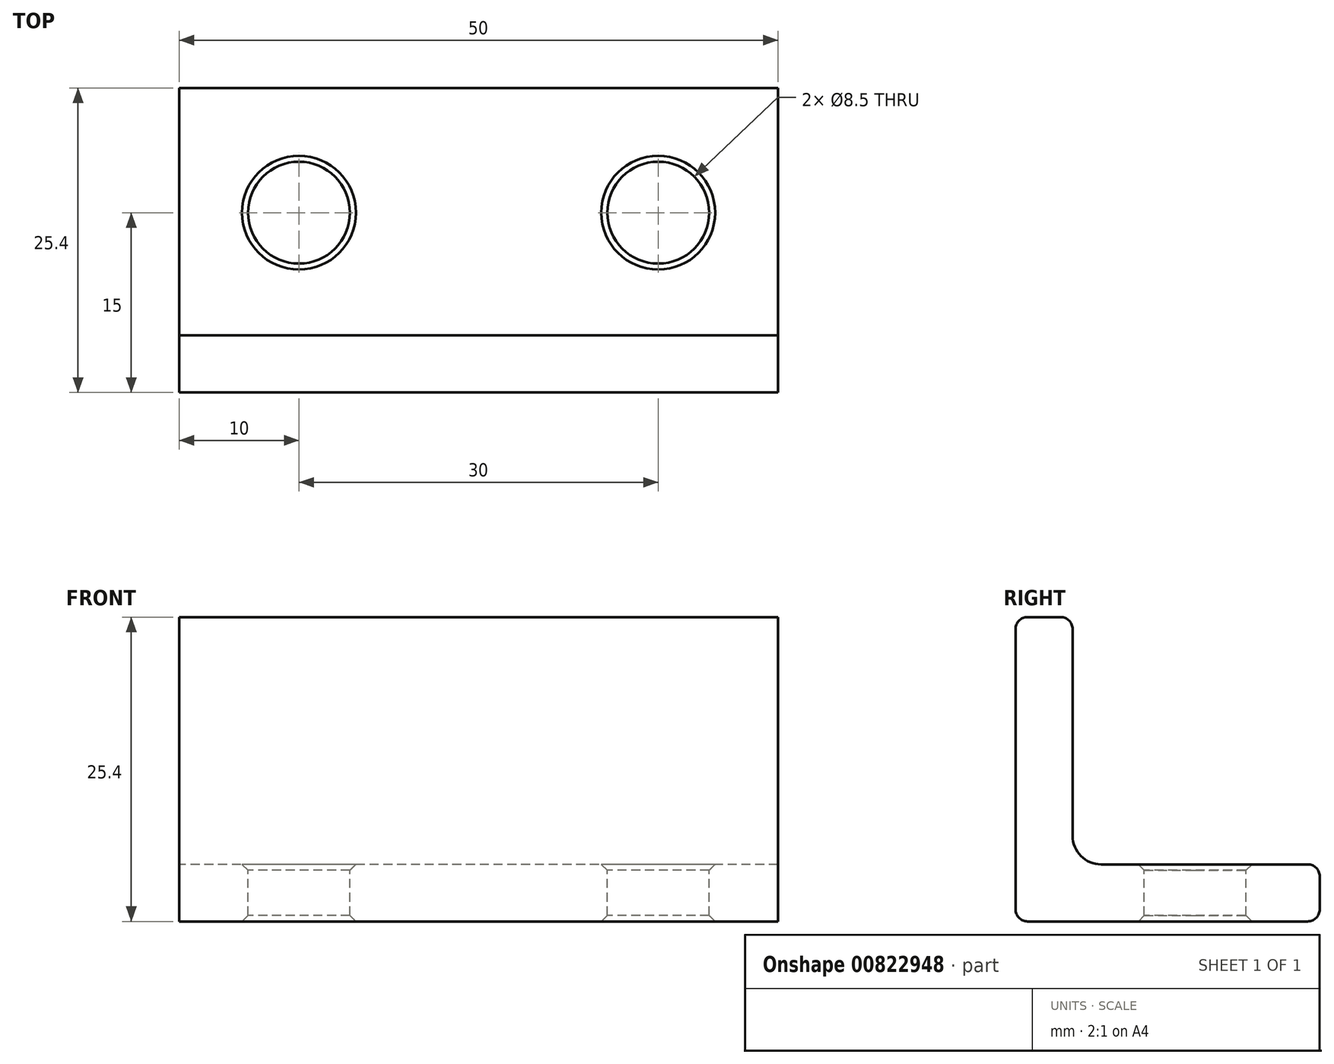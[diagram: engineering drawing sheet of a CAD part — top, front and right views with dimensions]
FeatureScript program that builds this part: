
annotation { "Feature Type Name" : "Feature", "Feature Type Description" : "" }
export const myFeature = defineFeature(function(context is Context, id is Id, definition is map)
    precondition{}
    {
        {
            var Q0;
            Q0=qCreatedBy(makeId("Right.planeOp"),FACE);
            var sketch = newSketch(context, id + "F0", { "sketchPlane" : qUnion([Q0])});
            skLineSegment(sketch, "E0", {"start": v(0, 0) * mm, "end": v(25.4, 0) * mm});
            skLineSegment(sketch, "E1", {"start": v(0, 0) * mm, "end": v(0, 25.4) * mm});
            skLineSegment(sketch, "E2", {"start": v(0, 25.4) * mm, "end": v(4.76, 25.4) * mm});
            skLineSegment(sketch, "E3", {"start": v(4.76, 25.4) * mm, "end": v(4.76, 4.76) * mm});
            skLineSegment(sketch, "E4", {"start": v(4.76, 4.76) * mm, "end": v(25.4, 4.76) * mm});
            skLineSegment(sketch, "E5", {"start": v(25.4, 4.76) * mm, "end": v(25.4, 0) * mm});
            skSolve(sketch);
        }
        {
            var Q0;
            Q0=qSketchRegion(id+"F0",true);
            extrude(context, id + "F1", {"entities" : qUnion([Q0]), "endBound" : BoundingType.SYMMETRIC, "depth" : 50 * mm, "offsetDistance" : 25 * mm});
        }
        {
            var Q0;
            Q0=makeQuery(id+"F1.opExtrude","SWEPT_EDGE",EDGE,{"disambiguationData":[OSD([sQuery(id+"F0.wireOp",EDGE,"E1"),sQuery(id+"F0.wireOp",EDGE,"E2")])]});
            var Q1;
            Q1=makeQuery(id+"F1.opExtrude","SWEPT_EDGE",EDGE,{"disambiguationData":[OSD([sQuery(id+"F0.wireOp",EDGE,"E2"),sQuery(id+"F0.wireOp",EDGE,"E3")])]});
            var Q2;
            Q2=makeQuery(id+"F1.opExtrude","SWEPT_EDGE",EDGE,{"disambiguationData":[OSD([sQuery(id+"F0.wireOp",EDGE,"E0"),sQuery(id+"F0.wireOp",EDGE,"E1")])]});
            var Q3;
            Q3=makeQuery(id+"F1.opExtrude","SWEPT_EDGE",EDGE,{"disambiguationData":[OSD([sQuery(id+"F0.wireOp",EDGE,"E4"),sQuery(id+"F0.wireOp",EDGE,"E5")])]});
            var Q4;
            Q4=makeQuery(id+"F1.opExtrude","SWEPT_EDGE",EDGE,{"disambiguationData":[OSD([sQuery(id+"F0.wireOp",EDGE,"E0"),sQuery(id+"F0.wireOp",EDGE,"E5")])]});
            fillet(context, id + "F2", {"entities" : qUnion([Q0, Q1, Q2, Q3, Q4]), "radius" : 1 * mm, "tangentPropagation" : true, "allowEdgeOverflow" : false});
        }
        {
            var Q0;
            Q0=makeQuery(id+"F1.opExtrude","SWEPT_EDGE",EDGE,{"disambiguationData":[OSD([sQuery(id+"F0.wireOp",EDGE,"E3"),sQuery(id+"F0.wireOp",EDGE,"E4")])]});
            fillet(context, id + "F3", {"entities" : qUnion([Q0]), "radius" : (3 * 25.4 / 16 / 2) * mm, "tangentPropagation" : true, "allowEdgeOverflow" : false});
        }
        {
            var Q0;
            Q0=makeQuery(id+"F1.opExtrude","SWEPT_FACE",FACE,{"disambiguationData":[OSD([sQuery(id+"F0.wireOp",EDGE,"E4")])]});
            var sketch = newSketch(context, id + "F4", { "sketchPlane" : qUnion([Q0])});
            skLineSegment(sketch, "E6.0", {"start": v(-25, 0) * mm, "end": v(25, 0) * mm, "construction": true});
            skLineSegment(sketch, "E7.0", {"start": v(-25, 1) * mm, "end": v(-25, 24.4) * mm, "construction": true});
            skCircle(sketch, "E8", {"center": v(-15, 15) * mm, "radius": 4.25 * mm});
            skLineSegment(sketch, "E9.0", {"start": v(-25, 25.4) * mm, "end": v(25, 25.4) * mm, "construction": true});
            skCircle(sketch, "E10.1.0.0", {"center": v(350, 15) * mm, "radius": 4.25 * mm, "construction": true});
            skCircle(sketch, "E10.2.0.0", {"center": v(715, 15) * mm, "radius": 4.25 * mm});
            skCircle(sketch, "E10.3.0.0", {"center": v(1080, 15) * mm, "radius": 4.25 * mm, "construction": true});
            skCircle(sketch, "E10.4.0.0", {"center": v(1445, 15) * mm, "radius": 4.25 * mm});
            skLineSegment(sketch, "E10.direction1", {"start": v(-15, 15) * mm, "end": v(5, 15) * mm, "construction": true});
            skLineSegment(sketch, "E11", {"start": v(0, 0) * mm, "end": v(0, -29.98) * mm, "construction": true});
            skCircle(sketch, "E12.MirrorC", {"center": v(15, 15) * mm, "radius": 4.25 * mm});
            skSolve(sketch);
        }
        {
            var Q0;
            Q0=qSketchRegion(id+"F4",true);
            extrude(context, id + "F5", {"entities" : qUnion([Q0]), "operationType" : NewBodyOperationType.REMOVE, "oppositeDirection" : true, "depth" : 25 * mm, "offsetDistance" : 25 * mm});
        }
        {
            var Q0;
            Q0=makeQuery(id+"F5.boolean.opBoolean","COPY",FACE,{"derivedFrom":makeQuery(id+"F5.opExtrude","SWEPT_FACE",FACE,{"disambiguationData":[OSD([sQuery(id+"F4.wireOp",EDGE,"E8")])]})});
            var Q1;
            Q1=makeQuery(id+"F5.boolean.opBoolean","COPY",FACE,{"derivedFrom":makeQuery(id+"F5.opExtrude","SWEPT_FACE",FACE,{"disambiguationData":[OSD([sQuery(id+"F4.wireOp",EDGE,"E10.1.0.0")])]})});
            var Q2;
            Q2=makeQuery(id+"F5.boolean.opBoolean","COPY",FACE,{"derivedFrom":makeQuery(id+"F5.opExtrude","SWEPT_FACE",FACE,{"disambiguationData":[OSD([sQuery(id+"F4.wireOp",EDGE,"E10.2.0.0")])]})});
            var Q3;
            Q3=makeQuery(id+"F5.boolean.opBoolean","COPY",FACE,{"derivedFrom":makeQuery(id+"F5.opExtrude","SWEPT_FACE",FACE,{"disambiguationData":[OSD([sQuery(id+"F4.wireOp",EDGE,"E10.3.0.0")])]})});
            var Q4;
            Q4=makeQuery(id+"F5.boolean.opBoolean","COPY",FACE,{"derivedFrom":makeQuery(id+"F5.opExtrude","SWEPT_FACE",FACE,{"disambiguationData":[OSD([sQuery(id+"F4.wireOp",EDGE,"E10.4.0.0")])]})});
            var Q5;
            Q5=makeQuery(id+"F5.boolean.opBoolean","COPY",FACE,{"derivedFrom":makeQuery(id+"F5.opExtrude","SWEPT_FACE",FACE,{"disambiguationData":[OSD([sQuery(id+"F4.wireOp",EDGE,"E12.MirrorC")])]})});
            chamfer(context, id + "F6", {"entities" : qUnion([Q0, Q1, Q2, Q3, Q4, Q5]), "width" : 0.5 * mm, "tangentPropagation" : true});
        }
        {
            var Q0;
            Q0=makeQuery(id+"F1.opExtrude","SWEPT_FACE",FACE,{"disambiguationData":[OSD([sQuery(id+"F0.wireOp",EDGE,"E1")])]});
            var sketch = newSketch(context, id + "F7", { "sketchPlane" : qUnion([Q0])});
            skLineSegment(sketch, "E13.0", {"start": v(-25, 1) * mm, "end": v(-25, 24.4) * mm, "construction": true});
            skLineSegment(sketch, "E14.0", {"start": v(25, 0) * mm, "end": v(-25, 0) * mm, "construction": true});
            skCircle(sketch, "E15", {"center": v(65, 20) * mm, "radius": 2.5 * mm});
            skLineSegment(sketch, "E16", {"start": v(0, 0) * mm, "end": v(0, -130.93) * mm, "construction": true});
            skCircle(sketch, "E17.MirrorC", {"center": v(-65, 20) * mm, "radius": 2.5 * mm});
            skSolve(sketch);
        }
        {
            var Q0;
            Q0=qSketchRegion(id+"F7",true);
            extrude(context, id + "F8", {"entities" : qUnion([Q0]), "operationType" : NewBodyOperationType.REMOVE, "oppositeDirection" : true, "depth" : 25 * mm, "offsetDistance" : 25 * mm});
        }
    });
